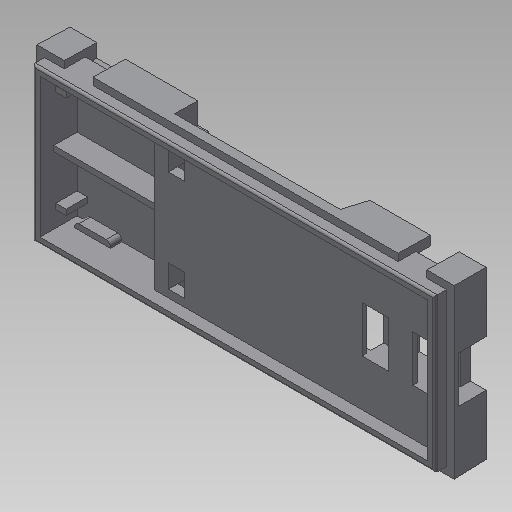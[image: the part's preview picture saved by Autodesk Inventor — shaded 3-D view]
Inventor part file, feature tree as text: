
AUTODESK INVENTOR PART (.ipt)
format: ipt  version: 2018 (Build 220112000, 112)  size: 522,240 bytes
history: native  units: mm
features: sketch x25, extrude x22, other x7, projected_geometry x5, loft x1, fillet x1
ambient origin geometry x8: Origin, YZ Plane, XZ Plane, XY Plane, X Axis, Y Axis, Z Axis, Center Point
bodies: Body1 (feature_tree)
feature tree (61):
  sketch  "Эскиз2"
  sketch  "Эскиз3"
  other  "РабПлоскость1"
  sketch  "Эскиз4"
  other  "РабПлоскость2"
  loft  "Лофт1"
  extrude  "Выдавливание2"  Depth=90.2mm
  extrude  "Выдавливание3"  Depth=0.174533mm
  extrude  "Выдавливание4"  Depth=0.174533mm
  extrude  "Выдавливание5"  Depth=0.174533mm
  extrude  "Выдавливание6"  Depth=0.174533mm
  sketch  "Эскиз11"
  extrude  "Выдавливание7"  Depth=36.3mm
  fillet  "Сопряжение1"  [1 undecoded]
  extrude  "Выдавливание8"  TaperAngle=0.0deg  [1 undecoded]
  extrude  "Выдавливание9"  TaperAngle=0.0deg  [1 undecoded]
  extrude  "Выдавливание10"  TaperAngle=0.0deg  [1 undecoded]
  other  "РабПлоскость3"
  other  "РабПлоскость4"
  extrude  "Выдавливание11"  Depth=86.8mm
  extrude  "Выдавливание12"  Depth=1.7mm
  other  "РабПлоскость5"
  extrude  "Выдавливание13"  Depth=1.7mm
  extrude  "Выдавливание14"  Depth=33.1mm
  extrude  "Выдавливание15"  Depth=1.6mm
  extrude  "Выдавливание16"  Depth=1.6mm
  extrude  "Выдавливание17"  Depth=1.0mm
  extrude  "Выдавливание18"  Depth=1.0mm
  extrude  "Выдавливание19"  Depth=1.0mm
  extrude  "Выдавливание20"  Depth=1.0mm
  other  "РабПлоскость6"
  extrude  "Выдавливание21"  Depth=2.5mm TaperAngle=0.0deg
  other  "РабПлоскость7"
  extrude  "Выдавливание22"  Depth=1.5mm
  extrude  "Выдавливание23"  Depth=1.5mm
  sketch  "Эскиз5"
  sketch  "Эскиз6"
  sketch  "Эскиз7"
  projected_geometry  "Спроецированная петля1"
  sketch  "Эскиз8"
  projected_geometry  "Спроецированная петля2"
  sketch  "Эскиз9"
  sketch  "Эскиз10"
  projected_geometry  "Спроецированная петля3"
  sketch  "Эскиз12"
  sketch  "Эскиз13"
  sketch  "Эскиз14"
  sketch  "Эскиз15"
  sketch  "Эскиз16"
  sketch  "Эскиз17"
  projected_geometry  "Спроецированная петля4"
  sketch  "Эскиз18"
  sketch  "Эскиз19"
  sketch  "Эскиз20"
  sketch  "Эскиз21"
  sketch  "Эскиз22"
  sketch  "Эскиз23"
  sketch  "Эскиз24"
  sketch  "Эскиз25"
  projected_geometry  "Спроецированная петля5"
  sketch  "Эскиз26"
note: 4 required parameter values undecoded (feature->parameter linkage not recoverable at this tier; creation-order binding heuristic only, values carry confidence <= 0.55)
